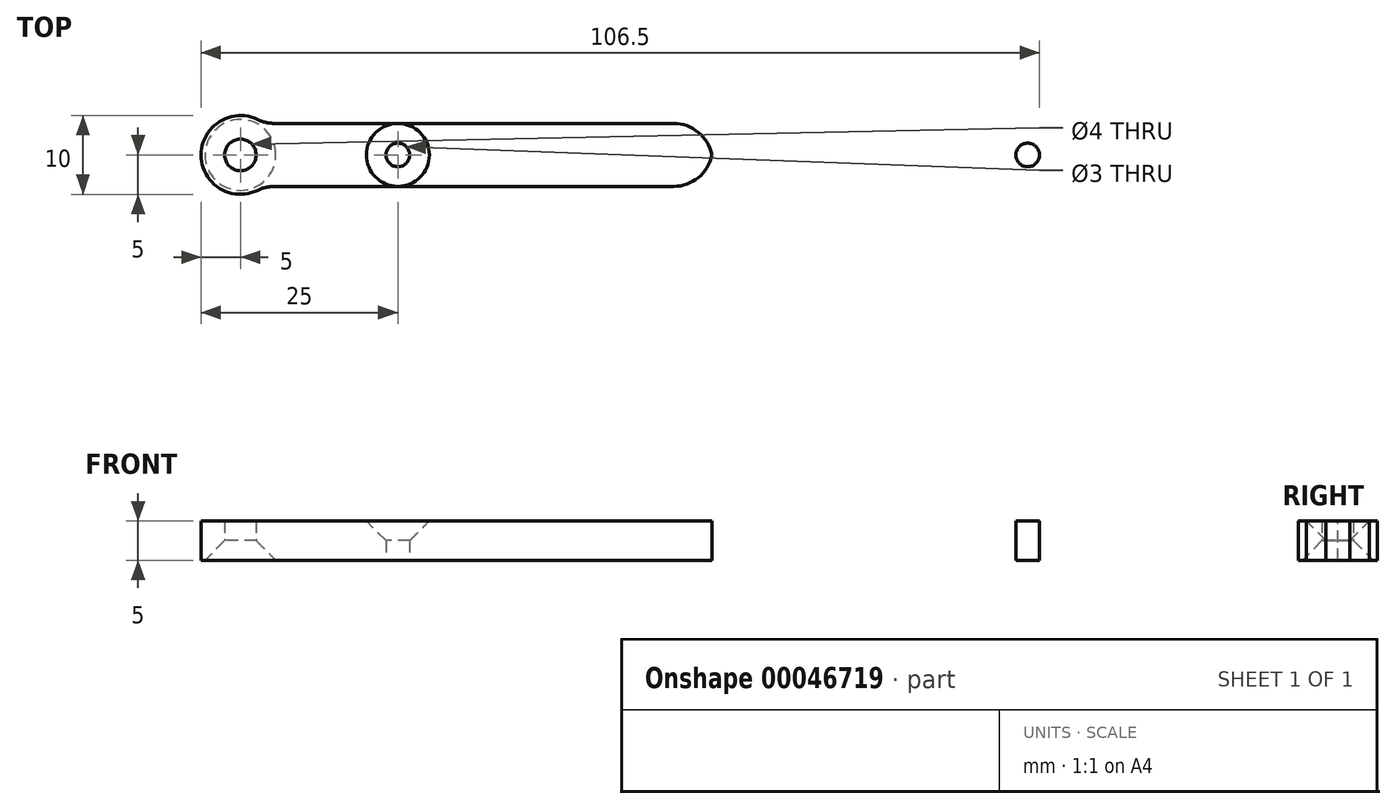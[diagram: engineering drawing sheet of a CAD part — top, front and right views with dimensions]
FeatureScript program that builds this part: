
annotation { "Feature Type Name" : "Feature", "Feature Type Description" : "" }
export const myFeature = defineFeature(function(context is Context, id is Id, definition is map)
    precondition{}
    {
        {
            var Q0;
            Q0=qCreatedBy(makeId("Top.planeOp"),FACE);
            var sketch = newSketch(context, id + "F0", { "sketchPlane" : qUnion([Q0])});
            skCircle(sketch, "E0", {"center": v(-60, 0) * mm, "radius": 2 * mm});
            skCircle(sketch, "E1", {"center": v(-40, 0) * mm, "radius": 1.5 * mm});
            skArc(sketch, "E2", {"start": v(-57, 4) * mm, "mid": v(-65, 0) * mm, "end": v(-57, -4) * mm});
            skLineSegment(sketch, "E3.bottom", {"start": v(-57, 4) * mm, "end": v(0, 4) * mm});
            skLineSegment(sketch, "E3.top", {"start": v(-57, -4) * mm, "end": v(0, -4) * mm});
            skLineSegment(sketch, "E3.right", {"start": v(0, 4) * mm, "end": v(0, -4) * mm});
            skCircle(sketch, "E4.MirrorC", {"center": v(40, 0) * mm, "radius": 1.5 * mm});
            skCircle(sketch, "E5.MirrorC", {"center": v(60, 0) * mm, "radius": 2 * mm});
            skArc(sketch, "E6.MirrorCS", {"start": v(57, 4) * mm, "mid": v(65, 0) * mm, "end": v(57, -4) * mm});
            skLineSegment(sketch, "E7.MirrorCS", {"start": v(57, 4) * mm, "end": v(0, 4) * mm});
            skLineSegment(sketch, "E8.MirrorCS", {"start": v(57, -4) * mm, "end": v(0, -4) * mm});
            skSolve(sketch);
        }
        {
            var Q0;
            Q0=makeQuery(id+"F0.imprint","IMPRINT",FACE,{"disambiguationData":[TD([[makeQuery(id+"F0.imprint","IMPRINT",EDGE,{"derivedFrom":sQuery(id+"F0.wireOp",EDGE,"E4.MirrorC")}),1.0]])]});
            var Q1;
            Q1=makeQuery(id+"F0.imprint","IMPRINT",FACE,{"disambiguationData":[TD([[makeQuery(id+"F0.imprint","IMPRINT",EDGE,{"derivedFrom":sQuery(id+"F0.wireOp",EDGE,"E0")}),-1.0]])]});
            extrude(context, id + "F1", {"entities" : qUnion([Q0, Q1]), "depth" : 5 * mm});
        }
        {
            var Q0;
            Q0=makeQuery(id+"F1.opExtrude","SWEPT_EDGE",EDGE,{"disambiguationData":[OSD([sQuery(id+"F0.wireOp",EDGE,"E2"),sQuery(id+"F0.wireOp",EDGE,"E3.bottom")])]});
            var Q1;
            Q1=makeQuery(id+"F1.opExtrude","SWEPT_EDGE",EDGE,{"disambiguationData":[OSD([sQuery(id+"F0.wireOp",EDGE,"E2"),sQuery(id+"F0.wireOp",EDGE,"E3.top")])]});
            var Q2;
            Q2=makeQuery(id+"F1.opExtrude","SWEPT_EDGE",EDGE,{"disambiguationData":[OSD([sQuery(id+"F0.wireOp",EDGE,"E6.MirrorCS"),sQuery(id+"F0.wireOp",EDGE,"E8.MirrorCS")])]});
            var Q3;
            Q3=makeQuery(id+"F1.opExtrude","SWEPT_EDGE",EDGE,{"disambiguationData":[OSD([sQuery(id+"F0.wireOp",EDGE,"E6.MirrorCS"),sQuery(id+"F0.wireOp",EDGE,"E7.MirrorCS")])]});
            fillet(context, id + "F2", {"entities" : qUnion([Q0, Q1, Q2, Q3]), "radius" : 5 * mm, "tangentPropagation" : true, "allowEdgeOverflow" : false});
        }
        {
            var Q0;
            Q0=makeQuery(id+"F1.opExtrude","CAP_EDGE",EDGE,{"disambiguationData":[OSD([sQuery(id+"F0.wireOp",EDGE,"E4.MirrorC")])],"isStart":false});
            var Q1;
            Q1=makeQuery(id+"F1.opExtrude","CAP_EDGE",EDGE,{"disambiguationData":[OSD([sQuery(id+"F0.wireOp",EDGE,"E1")])],"isStart":false});
            var Q2;
            Q2=makeQuery(id+"F1.opExtrude","CAP_EDGE",EDGE,{"disambiguationData":[OSD([sQuery(id+"F0.wireOp",EDGE,"E0")])],"isStart":true});
            var Q3;
            Q3=makeQuery(id+"F1.opExtrude","CAP_EDGE",EDGE,{"disambiguationData":[OSD([sQuery(id+"F0.wireOp",EDGE,"E5.MirrorC")])],"isStart":true});
            chamfer(context, id + "F3", {"entities" : qUnion([Q0, Q1, Q2, Q3]), "chamferType" : ChamferType.OFFSET_ANGLE, "width" : 2.5 * mm, "oppositeDirection" : false, "angle" : 45 * degree, "tangentPropagation" : true});
        }
    });
